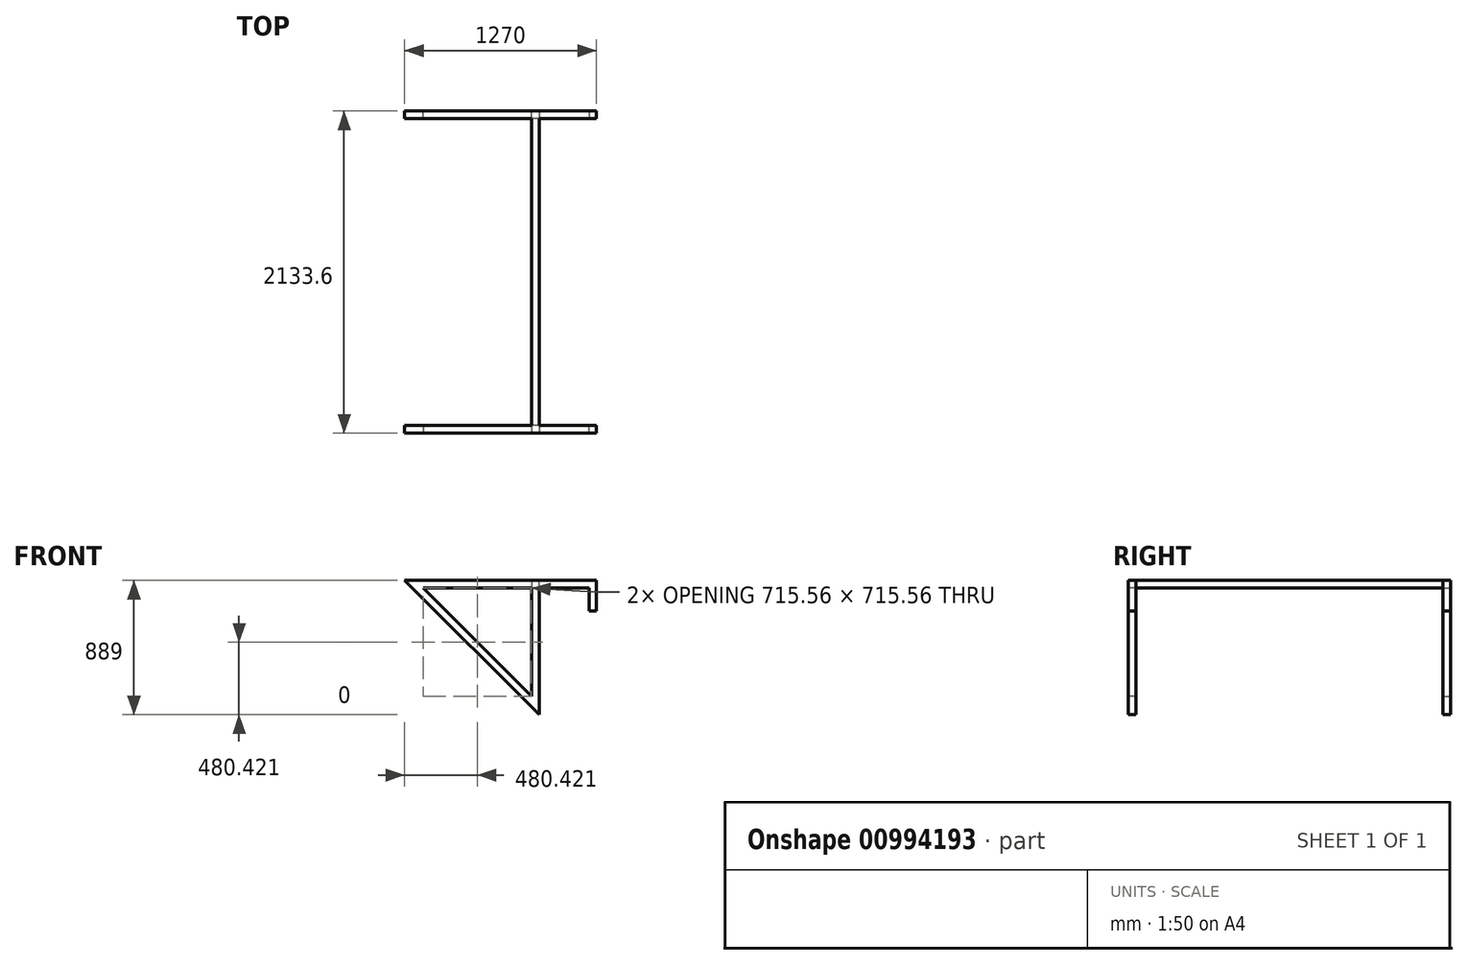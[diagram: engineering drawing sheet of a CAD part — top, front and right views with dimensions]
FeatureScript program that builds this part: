
annotation { "Feature Type Name" : "Feature", "Feature Type Description" : "" }
export const myFeature = defineFeature(function(context is Context, id is Id, definition is map)
    precondition{}
    {
        {
            var Q0;
            Q0=qCreatedBy(makeId("Front.planeOp"),FACE);
            var sketch = newSketch(context, id + "F0", { "sketchPlane" : qUnion([Q0])});
            skLineSegment(sketch, "E0", {"start": v(-203.2, 50.8) * mm, "end": v(685.8, 50.8) * mm});
            skLineSegment(sketch, "E1", {"start": v(685.8, 50.8) * mm, "end": v(685.8, -838.2) * mm});
            skLineSegment(sketch, "E2", {"start": v(-203.2, 50.8) * mm, "end": v(685.8, -838.2) * mm});
            skSolve(sketch);
        }
        {
            var Q0;
            Q0=makeQuery(id+"F0.imprint","IMPRINT",FACE,{"disambiguationData":[TD([[makeQuery(id+"F0.imprint","IMPRINT",EDGE,{"derivedFrom":sQuery(id+"F0.wireOp",EDGE,"E0")}),-1.0]])]});
            extrude(context, id + "F1", {"entities" : qUnion([Q0]), "depth" : 50.8 * mm, "offsetDistance" : 25.4 * mm});
        }
        {
            var Q0;
            Q0=makeQuery(id+"F1.opExtrude","CAP_FACE",FACE,{"disambiguationData":[OSD([sQuery(id+"F0.wireOp",EDGE,"E0"),sQuery(id+"F0.wireOp",EDGE,"E1"),sQuery(id+"F0.wireOp",EDGE,"E2")])],"isStart":true});
            var sketch = newSketch(context, id + "F2", { "sketchPlane" : qUnion([Q0])});
            skLineSegment(sketch, "E3.bottom", {"start": v(-685.8, 50.8) * mm, "end": v(-635, 50.8) * mm});
            skLineSegment(sketch, "E3.top", {"start": v(-685.8, 0) * mm, "end": v(-635, 0) * mm});
            skLineSegment(sketch, "E3.left", {"start": v(-685.8, 50.8) * mm, "end": v(-685.8, 0) * mm});
            skLineSegment(sketch, "E3.right", {"start": v(-635, 50.8) * mm, "end": v(-635, 0) * mm});
            skSolve(sketch);
        }
        {
            var Q0;
            Q0=qSketchRegion(id+"F2",true);
            extrude(context, id + "F3", {"entities" : qUnion([Q0]), "operationType" : NewBodyOperationType.ADD, "depth" : 1016 * mm, "offsetDistance" : 25.4 * mm});
        }
        {
            var Q0;
            Q0=makeQuery(id+"F0.imprint","IMPRINT",FACE,{"disambiguationData":[TD([[makeQuery(id+"F0.imprint","IMPRINT",EDGE,{"derivedFrom":sQuery(id+"F0.wireOp",EDGE,"E0")}),-1.0]])]});
            var sketch = newSketch(context, id + "F4", { "sketchPlane" : qUnion([Q0])});
            skLineSegment(sketch, "E4", {"start": v(685.8, -838.2) * mm, "end": v(649.79, -802.37) * mm});
            skLineSegment(sketch, "E5", {"start": v(649.79, -802.37) * mm, "end": v(685.8, -838.2) * mm});
            skLineSegment(sketch, "E6", {"start": v(685.8, -787.4) * mm, "end": v(685.8, -838.2) * mm});
            skLineSegment(sketch, "E7", {"start": v(685.8, -787.4) * mm, "end": v(649.79, -802.37) * mm});
            skSolve(sketch);
        }
        {
            var Q0;
            Q0=makeQuery(id+"FVzkL5AV8VG29R1_1.boolean.opBoolean","MERGE",FACE,{"derivedFrom":[makeQuery(id+"F3.boolean.opBoolean","MERGE",FACE,{"derivedFrom":[makeQuery(id+"F1.opExtrude","SWEPT_FACE",FACE,{"disambiguationData":[OSD([sQuery(id+"F0.wireOp",EDGE,"E1")])]}),makeQuery(id+"F3.opExtrude","SWEPT_FACE",FACE,{"disambiguationData":[OSD([sQuery(id+"F2.wireOp",EDGE,"E3.left")])]})]}),makeQuery(id+"FVzkL5AV8VG29R1_1.opExtrude","SWEPT_FACE",FACE,{"disambiguationData":[OSD([sQuery(id+"F4.wireOp",EDGE,"E6")])]})]});
            var sketch = newSketch(context, id + "F5", { "sketchPlane" : qUnion([Q0])});
            skLineSegment(sketch, "E8.bottom", {"start": v(0, 0) * mm, "end": v(-50.8, 0) * mm});
            skLineSegment(sketch, "E8.top", {"start": v(0, 50.8) * mm, "end": v(-50.8, 50.8) * mm});
            skLineSegment(sketch, "E8.left", {"start": v(0, 0) * mm, "end": v(0, 50.8) * mm});
            skLineSegment(sketch, "E8.right", {"start": v(-50.8, 0) * mm, "end": v(-50.8, 50.8) * mm});
            skSolve(sketch);
        }
        {
            var Q0;
            Q0=makeQuery(id+"F5.imprint","IMPRINT",FACE,{"disambiguationData":[TD([[makeQuery(id+"F5.imprint","IMPRINT",EDGE,{"derivedFrom":sQuery(id+"F5.wireOp",EDGE,"E8.bottom")}),-1.0]])]});
            extrude(context, id + "F6", {"entities" : qUnion([Q0]), "operationType" : NewBodyOperationType.ADD, "depth" : 381 * mm, "offsetDistance" : 25.4 * mm});
        }
        {
            var Q0;
            {var subQ0=sQuery(id+"F4.wireOp",EDGE,"E6");var subQ1=makeQuery(id+"FVzkL5AV8VG29R1_1.opExtrude","SWEPT_FACE",FACE,{"disambiguationData":[OSD([subQ0])]});var subQ4=makeQuery(id+"F3.opExtrude","SWEPT_FACE",FACE,{"disambiguationData":[OSD([sQuery(id+"F2.wireOp",EDGE,"E3.left")])]});var subQ5=sQuery(id+"F0.wireOp",EDGE,"E2");var subQ6=sQuery(id+"F0.wireOp",EDGE,"E1");var subQ8=makeQuery(id+"F1.opExtrude","SWEPT_FACE",FACE,{"disambiguationData":[OSD([subQ6])]});Q0=makeQuery(id+"F6.boolean.opBoolean","SPLIT",FACE,{"disambiguationData":[TD([makeQuery(id+"F1.opExtrude","SWEPT_FACE",FACE,{"disambiguationData":[OSD([subQ5])]})])],"derivedFrom":makeQuery(id+"FVzkL5AV8VG29R1_1.boolean.opBoolean","MERGE",FACE,{"derivedFrom":[makeQuery(id+"F3.boolean.opBoolean","MERGE",FACE,{"derivedFrom":[subQ8,subQ4]}),subQ1]})});}
            var sketch = newSketch(context, id + "F7", { "sketchPlane" : qUnion([Q0])});
            skLineSegment(sketch, "E9.bottom", {"start": v(-50.8, -838.2) * mm, "end": v(25.4, -838.2) * mm});
            skLineSegment(sketch, "E9.top", {"start": v(-50.8, -787.4) * mm, "end": v(25.4, -787.4) * mm});
            skLineSegment(sketch, "E9.left", {"start": v(-50.8, -838.2) * mm, "end": v(-50.8, -787.4) * mm});
            skLineSegment(sketch, "E9.right", {"start": v(25.4, -838.2) * mm, "end": v(25.4, -787.4) * mm});
            skSolve(sketch);
        }
        {
            var Q0;
            Q0=makeQuery(id+"Fc25ocHKRKDElpb_1.boolean.opBoolean","MERGE",FACE,{"derivedFrom":[makeQuery(id+"F6.boolean.opBoolean","MERGE",FACE,{"derivedFrom":[makeQuery(id+"F1.opExtrude","CAP_FACE",FACE,{"disambiguationData":[OSD([sQuery(id+"F0.wireOp",EDGE,"E0"),sQuery(id+"F0.wireOp",EDGE,"E1"),sQuery(id+"F0.wireOp",EDGE,"E2")])],"isStart":false}),makeQuery(id+"F6.opExtrude","SWEPT_FACE",FACE,{"disambiguationData":[OSD([sQuery(id+"F5.wireOp",EDGE,"E8.right")])]})]}),makeQuery(id+"Fc25ocHKRKDElpb_1.opExtrude","SWEPT_FACE",FACE,{"disambiguationData":[OSD([sQuery(id+"F7.wireOp",EDGE,"E9.left")])]})]});
            var sketch = newSketch(context, id + "F8", { "sketchPlane" : qUnion([Q0])});
            skLineSegment(sketch, "E10", {"start": v(635, 0) * mm, "end": v(-80.56, 0) * mm});
            skLineSegment(sketch, "E11", {"start": v(635, 0) * mm, "end": v(635, -715.56) * mm});
            skLineSegment(sketch, "E12", {"start": v(-80.56, 0) * mm, "end": v(635, -715.56) * mm});
            skSolve(sketch);
        }
        {
            var Q0;
            Q0=makeQuery(id+"F8.imprint","IMPRINT",FACE,{"disambiguationData":[TD([[makeQuery(id+"F8.imprint","IMPRINT",EDGE,{"derivedFrom":sQuery(id+"F8.wireOp",EDGE,"E10")}),1.0]])]});
            extrude(context, id + "F9", {"entities" : qUnion([Q0]), "operationType" : NewBodyOperationType.REMOVE, "endBound" : BoundingType.THROUGH_ALL, "oppositeDirection" : true, "depth" : 25.4 * mm, "offsetDistance" : 25.4 * mm});
        }
        {
            var Q0;
            Q0=makeQuery(id+"F3.opExtrude","CAP_FACE",FACE,{"disambiguationData":[OSD([sQuery(id+"F2.wireOp",EDGE,"E3.bottom"),sQuery(id+"F2.wireOp",EDGE,"E3.top"),sQuery(id+"F2.wireOp",EDGE,"E3.left"),sQuery(id+"F2.wireOp",EDGE,"E3.right")])],"isStart":false});
            var Q1;
            Q1=makeQuery(id+"F3.opExtrude","CAP_VERTEX",VERTEX,{"disambiguationData":[OSD([sQuery(id+"F0.wireOp",EDGE,"E1"),sQuery(id+"F2.wireOp",EDGE,"E3.top"),sQuery(id+"F2.wireOp",EDGE,"E3.left")])],"isStart":false});
            cPlane(context, id + "F10", {"entities" : qUnion([Q0, Q1]), "cplaneType" : CPlaneType.PLANE_POINT, "offset" : 25.4 * mm, "width" : 152.4 * mm, "height" : 152.4 * mm});
        }
        {
            var Q0;
            Q0=makeQuery(id+"F6.opExtrude","SWEPT_FACE",FACE,{"disambiguationData":[OSD([sQuery(id+"F5.wireOp",EDGE,"E8.bottom")])]});
            var sketch = newSketch(context, id + "F11", { "sketchPlane" : qUnion([Q0])});
            skLineSegment(sketch, "E13.bottom", {"start": v(1066.8, 50.8) * mm, "end": v(1016, 50.8) * mm});
            skLineSegment(sketch, "E13.top", {"start": v(1066.8, 0) * mm, "end": v(1016, 0) * mm});
            skLineSegment(sketch, "E13.left", {"start": v(1066.8, 50.8) * mm, "end": v(1066.8, 0) * mm});
            skLineSegment(sketch, "E13.right", {"start": v(1016, 50.8) * mm, "end": v(1016, 0) * mm});
            skSolve(sketch);
        }
        {
            var Q0;
            Q0=makeQuery(id+"F11.imprint","IMPRINT",FACE,{"disambiguationData":[TD([[makeQuery(id+"F11.imprint","IMPRINT",EDGE,{"derivedFrom":sQuery(id+"F11.wireOp",EDGE,"E13.bottom")}),1.0]])]});
            extrude(context, id + "F12", {"entities" : qUnion([Q0]), "operationType" : NewBodyOperationType.ADD, "depth" : 152.4 * mm, "offsetDistance" : 25.4 * mm});
        }
        {
            var Q0;
            Q0=makeQuery(id+"F1.opExtrude","SWEPT_BODY",BODY,{"disambiguationData":[OSD([sQuery(id+"F0.wireOp",EDGE,"E0"),sQuery(id+"F0.wireOp",EDGE,"E1"),sQuery(id+"F0.wireOp",EDGE,"E2")])]});
            var Q1;
            Q1=qCreatedBy(id+"F10.planeOp",FACE);
            mirror(context, id + "F13", {"operationType" : NewBodyOperationType.ADD, "entities" : qUnion([Q0]), "mirrorPlane" : qUnion([Q1])});
        }
    });
